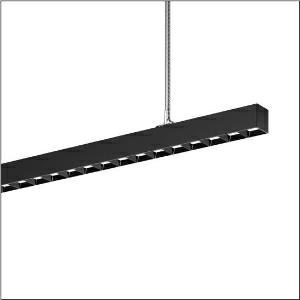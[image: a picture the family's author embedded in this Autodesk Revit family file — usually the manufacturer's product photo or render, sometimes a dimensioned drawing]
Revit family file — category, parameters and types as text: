
# Revit family: silica_r__21_51mx32dc4dbb_b922
name_source: partatom
category: Lighting Fixtures
units: mm (PartAtom-declared; Revit-internal decimal feet)

## family parameters
Cut with Voids When Loaded = No
Host = Face
Light Source = No
Part Type = Normal
Room Calculation Point = No
Round Connector Dimension = Use Diameter
Shared = No

## types (1)
- --- (1 x LED, 18230 lm, 105.8 W, 4000K)
    Apparent Load = 106 VA
    CIE Flux Codes = 86 99 100 59 100
    Color Rendering = 80
    Color Temperature = 4000K
    Default Elevation = 1800 mm
    Description = Silica® 21, office luminaire, primary light control with darklight reflector, of PMMA, black, CAT 2 (L<= 3000cd/m²), light emission: direct/indirect distribution, primary light characteristic: symmetric, installation type: suspended mounting, LED, rated luminous flux: 18.230lm, luminous efficacy: 172lm/W, light colour: 840, colour temperature: 4000K, with terminal, 3+2-pole, max. 2.5mm², mains connection: 220..240V, AC, 50/60Hz, rated input power: 105.8W, luminaire housing, of aluminium, jet black (RAL 9005), length: 3.004mm, width: 53mm, height: 53mm, protection rating (complete): IP20, insulation class (complete): insulation class I (protective earthing), certification: CE, permissible operating ambient temperature: 0..+35°C, standard: EN 50419, packaging unit: 1 piece
    Height = 53 mm
    Lamp = 1 x LED
    Lamp Light Flux = 18230 lm
    Lamp Power = 105.8 W
    Lamp count = 1
    Length = 3004 mm
    Luminous efficacy = 172 lm/W
    Manufacturer = Siteco
    ModVariant = No
    Model = 51MX32DC4DBB
    Mounting Place = Ceiling
    Mounting Type = Pendant
    Number of Poles = 1
    OnlyDefault = Yes
    Power Factor = 1
    Product Name = Silica® 21
    Product group = office luminaire | ceiling pendant
    ProductGroupID = 902
    Protection Class = Protection class I
    Protection Degree = IP 20
    RLX_Detail_Level = 1
    RLX_Emergency_Light_Flux = 0 lm
    RLX_Emergency_Type = 0
    RLX_Emergency_Type_DB = No
    RlxData = <blob elided: 67049 chars, md5=99d9a60e>
    Socket = socket
    Standby Power = 0 W
    System Light Flux = 18230 lm
    System Power = 106 W
    Type Comments = factory setting: luminous flux: 100 % | dim-lin: 254 | 366 mA
    Type Image = l_1335852.jpg
    URL = http://relux.com
    VarID = @adj_091613
    Voltage = 0 V
    Weight = 0.00 kg
    Width = 53 mm

## geometry (parser evidence)
native form markers: Blend x4, Sweep x13
no freeform markers — native parametric forms only
